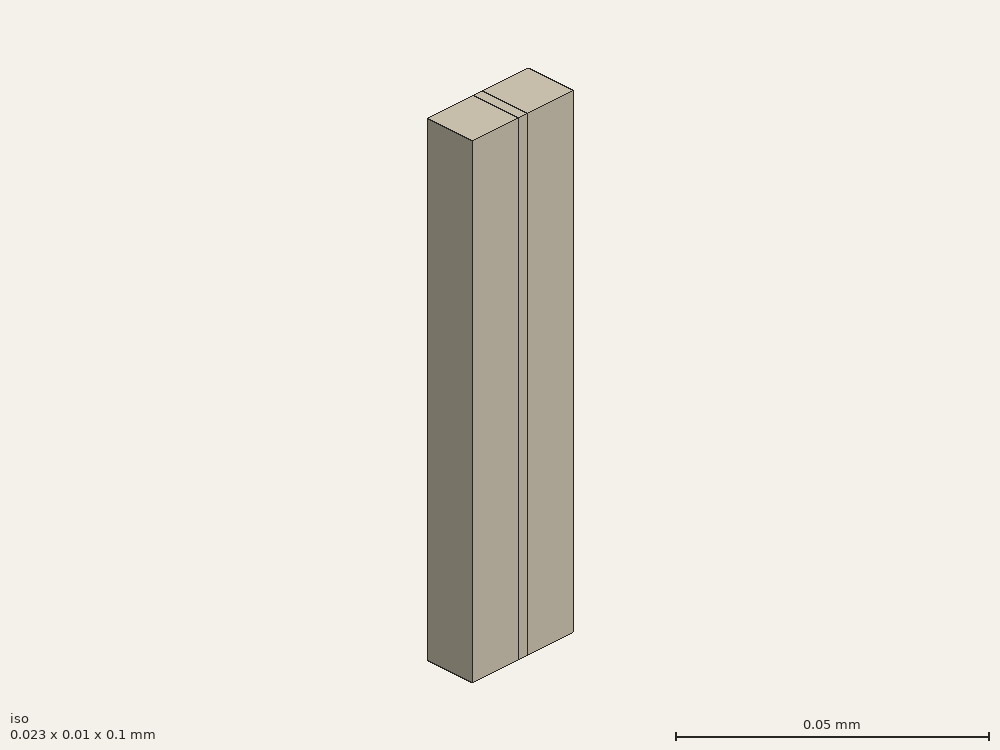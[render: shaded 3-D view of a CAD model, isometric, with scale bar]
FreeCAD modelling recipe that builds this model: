
FCSTD DOCUMENT  (FreeCAD 0.21R33694 (Git))
Label: straight-loaded
License: All rights reserved
LicenseURL: http://en.wikipedia.org/wiki/All_rights_reserved
objects: Part::Part2DObjectPython×10, App::FeaturePython×8, Part::Extrusion×2, Part::FeaturePython×2
note: 14 computed .brp shape members not serialized (recipe doc carries the construction recipe); baked Part::Feature solids carry a one-line shape summary decoded from their .brp

FEATURE [Part::Part2DObjectPython] Rectangle  # Draft 2D object (typed FeaturePython)
  Area = 232.258
  ChamferSize = 0
  Columns = 1
  FilletRadius = 0
  Height = 10.16
  Length = 22.86
  MakeFace = true
  Placement = pos=(-11.43,-5.08,0) rot=(0,0,1;0rad)
  Rows = 1
FEATURE [Part::Part2DObjectPython] Rectangle001  label="_Pport1"  # Draft 2D object (typed FeaturePython)
  Area = 0.000232258
  ChamferSize = 0
  Columns = 1
  FilletRadius = 0
  Height = 0.01016
  Length = 0.02286
  MakeFace = true
  Placement = pos=(-0.01143,-0.00508,0.1) rot=(0,0,1;0rad)
  Rows = 1
FEATURE [Part::Part2DObjectPython] Line  label="_Pv1"  # Draft 2D object (typed FeaturePython)
  Area = 0
  ChamferSize = 0
  Closed = false
  End = (-1.8e-15,0.00508,0.1)
  FilletRadius = 0
  Length = 0.01016
  MakeFace = true
  Placement = pos=(0,-0.00508,0.1) rot=(0,0,1;0rad)
  Points = (2) [(0,0,0),(-1.77605e-15,0.01016,0)]
  Start = (0,-0.00508,0.1)
  Subdivisions = 0
FEATURE [Part::Part2DObjectPython] Rectangle002  label="_Pport2"  # Draft 2D object (typed FeaturePython)
  Area = 0.000232258
  ChamferSize = 0
  Columns = 1
  FilletRadius = 0
  Height = 0.01016
  Length = 0.02286
  MakeFace = true
  Placement = pos=(-0.01143,-0.00508,0) rot=(0,0,1;0rad)
  Rows = 1
FEATURE [Part::Part2DObjectPython] Line001  label="_Pv2"  # Draft 2D object (typed FeaturePython)
  Area = 0
  ChamferSize = 0
  Closed = false
  End = (0,0.00508,0)
  FilletRadius = 0
  Length = 0.01016
  MakeFace = true
  Placement = pos=(0,-0.00508,0) rot=(0,0,1;0rad)
  Points = (2) [(0,0,0),(3.1106e-19,0.01016,0)]
  Start = (0,-0.00508,0)
  Subdivisions = 0
FEATURE [App::FeaturePython] Text  label="_Sinput(PV){port1}"  # WARN: FeaturePython — macro-defined, semantics opaque (R4)
  Placement = pos=(0.0413747,-0.017509,0) rot=(0,0,1;0rad)
  Text = .
FEATURE [App::FeaturePython] Text001  label="_Soutput(PV){port2}"  # WARN: FeaturePython — macro-defined, semantics opaque (R4)
  Placement = pos=(0.0413747,-0.017509,0) rot=(0,0,1;0rad)
  Text = .
FEATURE [App::FeaturePython] Text002  label="_Linput(1,voltage){v1}"  # WARN: FeaturePython — macro-defined, semantics opaque (R4)
  Placement = pos=(0.0413747,-0.017509,0) rot=(0,0,1;0rad)
  Text = .
FEATURE [App::FeaturePython] Text003  label="_Loutput(2,voltage){v2}"  # WARN: FeaturePython — macro-defined, semantics opaque (R4)
  Placement = pos=(0.0413747,-0.017509,0) rot=(0,0,1;0rad)
  Text = .
FEATURE [Part::Extrusion] Extrude
  Base = -> Rectangle
  Dir = (0,0,1)
  DirMode = 2
  FaceMakerClass = Part::FaceMakerBullseye
  LengthFwd = 100
  LengthRev = 0
  Solid = false
  Symmetric = false
FEATURE [Part::Part2DObjectPython] Rectangle004  # Draft 2D object (typed FeaturePython)
  Area = 20.32
  ChamferSize = 0
  Columns = 1
  FilletRadius = 0
  Height = 2
  Length = 10.16
  MakeFace = true
  Placement = pos=(-1,-5.08,0) rot=(0.707107,0.707107,0;3.14159rad)
  Rows = 1
FEATURE [Part::Extrusion] Extrude001
  Base = -> Rectangle004
  Dir = (1e-16,-1e-16,-1)
  DirMode = 2
  FaceMakerClass = Part::FaceMakerBullseye
  LengthFwd = -100
  LengthRev = 0
  Solid = false
  Symmetric = false
FEATURE [Part::FeaturePython] BooleanFragments  # WARN: FeaturePython — macro-defined, semantics opaque (R4)
  Mode = 0
  Objects = -> [Extrude,Extrude001]
  Tolerance = 0
FEATURE [Part::FeaturePython] Clone  label="scaled"  # Draft clone (typed FeaturePython)
  AttacherType = Attacher::AttachEngine3D
  Fuse = false
  Objects = -> [BooleanFragments]
  Scale = (0.001,0.001,0.001)
FEATURE [Part::Part2DObjectPython] Rectangle005  label="_Pside1"  # Draft 2D object (typed FeaturePython)
  Area = 0.002286
  ChamferSize = 0
  Columns = 1
  FilletRadius = 0
  Height = 0.1
  Length = 0.02286
  MakeFace = true
  Placement = pos=(-0.01143,-0.00508,0) rot=(1,0,0;1.5708rad)
  Rows = 1
FEATURE [Part::Part2DObjectPython] Rectangle006  label="_Pside3"  # Draft 2D object (typed FeaturePython)
  Area = 0.002286
  ChamferSize = 0
  Columns = 1
  FilletRadius = 0
  Height = 0.1
  Length = 0.02286
  MakeFace = true
  Placement = pos=(-0.01143,0.00508,0) rot=(1,0,0;1.5708rad)
  Rows = 1
FEATURE [Part::Part2DObjectPython] Rectangle007  label="_Pside2"  # Draft 2D object (typed FeaturePython)
  Area = 0.001016
  ChamferSize = 0
  Columns = 1
  FilletRadius = 0
  Height = 0.1
  Length = 0.01016
  MakeFace = true
  Placement = pos=(0.01143,-0.00508,0) rot=(0.57735,0.57735,0.57735;2.0944rad)
  Rows = 1
FEATURE [Part::Part2DObjectPython] Rectangle008  label="_Pside4"  # Draft 2D object (typed FeaturePython)
  Area = 0.001016
  ChamferSize = 0
  Columns = 1
  FilletRadius = 0
  Height = 0.1
  Length = 0.01016
  MakeFace = true
  Placement = pos=(-0.01143,-0.00508,0) rot=(0.57735,0.57735,0.57735;2.0944rad)
  Rows = 1
FEATURE [App::FeaturePython] Text004  label="_BCu1(SI,copper){side1}"  # WARN: FeaturePython — macro-defined, semantics opaque (R4)
  Placement = pos=(0.0413747,-0.017509,0) rot=(0,0,1;0rad)
  Text = .
FEATURE [App::FeaturePython] Text005  label="_BCu2(SI,copper){side2}"  # WARN: FeaturePython — macro-defined, semantics opaque (R4)
  Placement = pos=(0.0413747,-0.017509,0) rot=(0,0,1;0rad)
  Text = .
FEATURE [App::FeaturePython] Text006  label="_BCu3(SI,copper){side3}"  # WARN: FeaturePython — macro-defined, semantics opaque (R4)
  Placement = pos=(0.0413747,-0.017509,0) rot=(0,0,1;0rad)
  Text = .
FEATURE [App::FeaturePython] Text007  label="_BCu4(SI,copper){side4}"  # WARN: FeaturePython — macro-defined, semantics opaque (R4)
  Placement = pos=(0.0413747,-0.017509,0) rot=(0,0,1;0rad)
  Text = .
